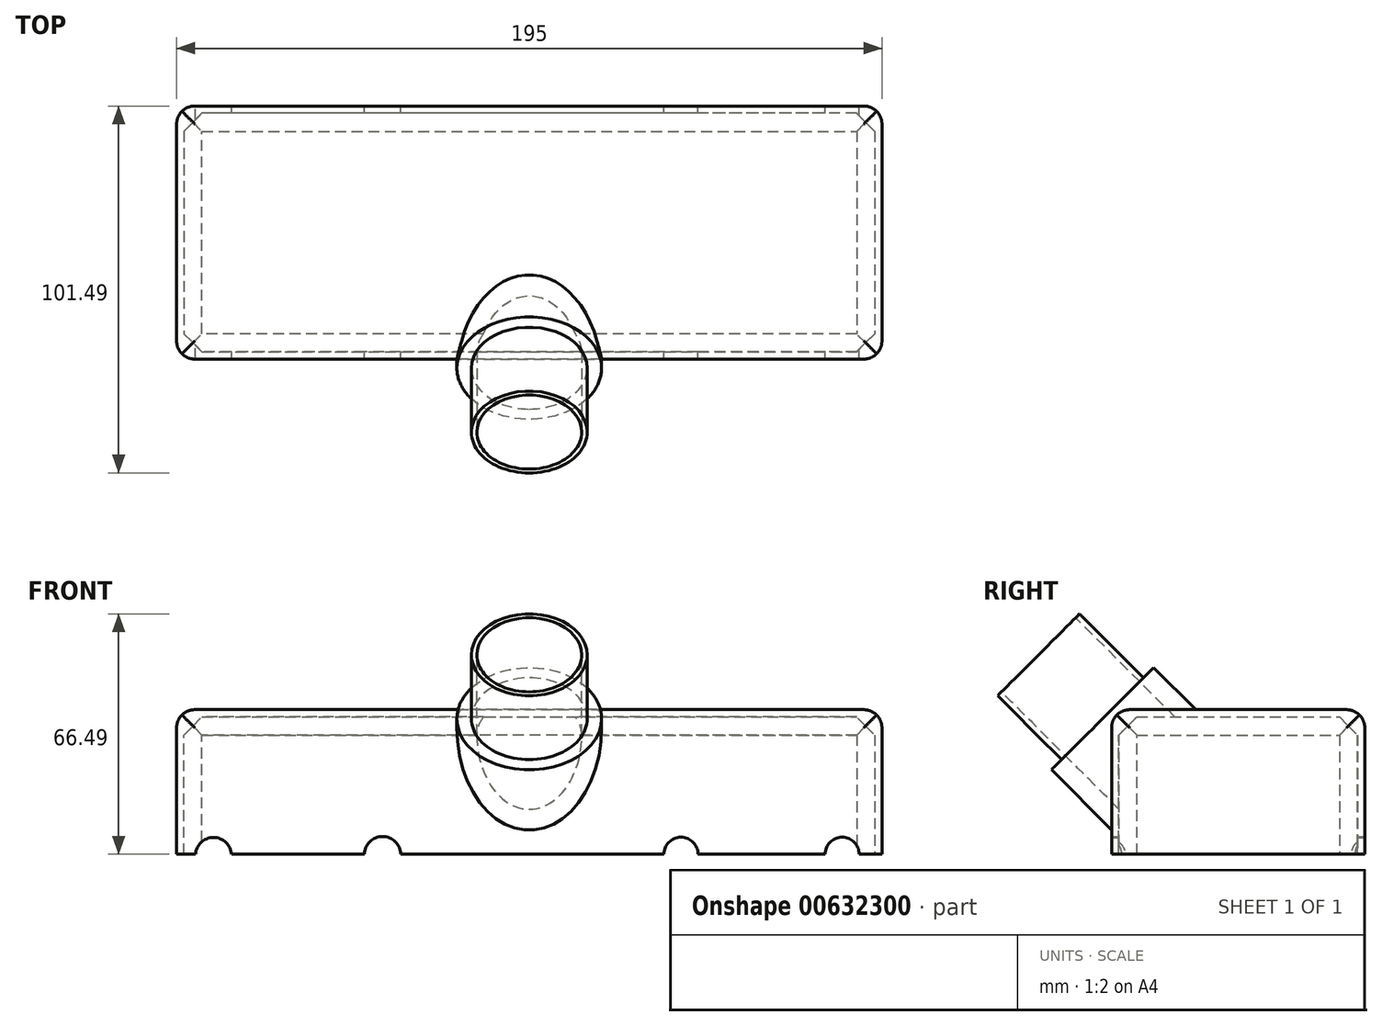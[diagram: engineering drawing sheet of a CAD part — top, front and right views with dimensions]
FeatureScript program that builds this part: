
annotation { "Feature Type Name" : "Feature", "Feature Type Description" : "" }
export const myFeature = defineFeature(function(context is Context, id is Id, definition is map)
    precondition{}
    {
        {
            var Q0;
            Q0=qCreatedBy(makeId("Top.planeOp"),FACE);
            var sketch = newSketch(context, id + "F0", { "sketchPlane" : qUnion([Q0])});
            skLineSegment(sketch, "E0.bottom", {"start": v(-97.5, -35) * mm, "end": v(97.5, -35) * mm});
            skLineSegment(sketch, "E0.top", {"start": v(-97.5, 35) * mm, "end": v(97.5, 35) * mm});
            skLineSegment(sketch, "E0.left", {"start": v(-97.5, -35) * mm, "end": v(-97.5, 35) * mm});
            skLineSegment(sketch, "E0.right", {"start": v(97.5, -35) * mm, "end": v(97.5, 35) * mm});
            skPoint(sketch, "E0.middle", {"position": v(0, 0) * mm});
            skSolve(sketch);
        }
        {
            var Q0;
            Q0=makeQuery(id+"F0.imprint","IMPRINT",FACE,{"disambiguationData":[TD([[makeQuery(id+"F0.imprint","IMPRINT",EDGE,{"derivedFrom":sQuery(id+"F0.wireOp",EDGE,"E0.bottom")}),1.0]])]});
            extrude(context, id + "F1", {"entities" : qUnion([Q0]), "depth" : 40 * mm, "offsetDistance" : 25 * mm});
        }
        {
            var Q0;
            Q0=makeQuery(id+"F1.opExtrude","CAP_EDGE",EDGE,{"disambiguationData":[OSD([sQuery(id+"F0.wireOp",EDGE,"E0.bottom")])],"isStart":false});
            cPlane(context, id + "F2", {"entities" : qUnion([Q0]), "cplaneType" : CPlaneType.LINE_ANGLE, "offset" : 25 * mm, "angle" : 45 * degree, "oppositeDirection" : true, "width" : 150 * mm, "height" : 150 * mm});
        }
        {
            var Q0;
            Q0=qCreatedBy(id+"F2.planeOp",FACE);
            var sketch = newSketch(context, id + "F3", { "sketchPlane" : qUnion([Q0])});
            skCircle(sketch, "E1", {"center": v(0, 0) * mm, "radius": 20 * mm});
            skSolve(sketch);
        }
        {
            var Q0;
            Q0=makeQuery(id+"F3.imprint","IMPRINT",FACE,{"disambiguationData":[TD([[makeQuery(id+"F3.imprint","IMPRINT",EDGE,{"derivedFrom":sQuery(id+"F3.wireOp",EDGE,"E1")}),1.0]])]});
            extrude(context, id + "F4", {"entities" : qUnion([Q0]), "operationType" : NewBodyOperationType.ADD, "depth" : 30 * mm, "offsetDistance" : 25 * mm});
        }
        {
            var Q0;
            Q0=makeQuery(id+"F4.opExtrude","CAP_FACE",FACE,{"disambiguationData":[OSD([sQuery(id+"F3.wireOp",EDGE,"E1")])],"isStart":true});
            var sketch = newSketch(context, id + "F5", { "sketchPlane" : qUnion([Q0])});
            skCircle(sketch, "E2", {"center": v(0, 0) * mm, "radius": 16 * mm});
            skSolve(sketch);
        }
        {
            var Q0;
            Q0=makeQuery(id+"F5.imprint","IMPRINT",FACE,{"disambiguationData":[TD([[makeQuery(id+"F5.imprint","IMPRINT",EDGE,{"derivedFrom":sQuery(id+"F5.wireOp",EDGE,"E2")}),1.0]])]});
            var Q1;
            Q1=makeQuery(id+"F5.imprint","IMPRINT",FACE,{"disambiguationData":[TD([[makeQuery(id+"F5.imprint","IMPRINT",EDGE,{"derivedFrom":sQuery(id+"F5.wireOp",EDGE,"E2")}),-1.0]])]});
            extrude(context, id + "F6", {"entities" : qUnion([Q0, Q1]), "operationType" : NewBodyOperationType.ADD, "depth" : 25 * mm, "offsetDistance" : 25 * mm});
        }
        {
            var Q0;
            Q0=makeQuery(id+"F6.opExtrude","CAP_FACE",FACE,{"disambiguationData":[OSD([sQuery(id+"F3.wireOp",EDGE,"E1")])],"isStart":false});
            var sketch = newSketch(context, id + "F7", { "sketchPlane" : qUnion([Q0])});
            skCircle(sketch, "E3", {"center": v(0, 0) * mm, "radius": 16 * mm});
            skSolve(sketch);
        }
        {
            var Q0;
            Q0=makeQuery(id+"F7.imprint","IMPRINT",FACE,{"disambiguationData":[TD([[makeQuery(id+"F7.imprint","IMPRINT",EDGE,{"derivedFrom":sQuery(id+"F7.wireOp",EDGE,"E3")}),-1.0]])]});
            extrude(context, id + "F8", {"entities" : qUnion([Q0]), "operationType" : NewBodyOperationType.REMOVE, "oppositeDirection" : true, "depth" : 35 * mm, "offsetDistance" : 25 * mm});
        }
        {
            var Q0;
            Q0=makeQuery(id+"F8.boolean.opBoolean","COPY",FACE,{"derivedFrom":makeQuery(id+"F8.opExtrude","CAP_FACE",FACE,{"disambiguationData":[OSD([sQuery(id+"F3.wireOp",EDGE,"E1"),sQuery(id+"F7.wireOp",EDGE,"E3")])],"isStart":false})});
            extrude(context, id + "F9", {"entities" : qUnion([Q0]), "operationType" : NewBodyOperationType.ADD, "depth" : 10 * mm, "offsetDistance" : 25 * mm});
        }
        {
            var Q0;
            Q0=makeQuery(id+"F6.opExtrude","CAP_FACE",FACE,{"disambiguationData":[OSD([sQuery(id+"F3.wireOp",EDGE,"E1")])],"isStart":false});
            var sketch = newSketch(context, id + "F10", { "sketchPlane" : qUnion([Q0])});
            skCircle(sketch, "E4", {"center": v(0, 0) * mm, "radius": 14.5 * mm});
            skSolve(sketch);
        }
        {
            var Q0;
            Q0=makeQuery(id+"F10.imprint","IMPRINT",FACE,{"disambiguationData":[TD([[makeQuery(id+"F10.imprint","IMPRINT",EDGE,{"derivedFrom":sQuery(id+"F10.wireOp",EDGE,"E4")}),1.0]])]});
            extrude(context, id + "F11", {"entities" : qUnion([Q0]), "operationType" : NewBodyOperationType.REMOVE, "endBound" : BoundingType.THROUGH_ALL, "oppositeDirection" : true, "depth" : 25 * mm, "offsetDistance" : 25 * mm});
        }
        {
            var Q0;
            Q0=makeQuery(id+"F1.opExtrude","CAP_FACE",FACE,{"disambiguationData":[OSD([sQuery(id+"F0.wireOp",EDGE,"E0.bottom"),sQuery(id+"F0.wireOp",EDGE,"E0.top"),sQuery(id+"F0.wireOp",EDGE,"E0.left"),sQuery(id+"F0.wireOp",EDGE,"E0.right")])],"isStart":true});
            var sketch = newSketch(context, id + "F12", { "sketchPlane" : qUnion([Q0])});
            skLineSegment(sketch, "E5.bottom", {"start": v(95.5, -33) * mm, "end": v(-95.5, -33) * mm});
            skLineSegment(sketch, "E5.top", {"start": v(95.5, 33) * mm, "end": v(-95.5, 33) * mm});
            skLineSegment(sketch, "E5.left", {"start": v(95.5, -33) * mm, "end": v(95.5, 33) * mm});
            skLineSegment(sketch, "E5.right", {"start": v(-95.5, -33) * mm, "end": v(-95.5, 33) * mm});
            skPoint(sketch, "E5.middle", {"position": v(0, 0) * mm});
            skSolve(sketch);
        }
        {
            var Q0;
            Q0=makeQuery(id+"F12.imprint","IMPRINT",FACE,{"disambiguationData":[TD([[makeQuery(id+"F12.imprint","IMPRINT",EDGE,{"derivedFrom":sQuery(id+"F12.wireOp",EDGE,"E5.bottom")}),-1.0]])]});
            extrude(context, id + "F13", {"entities" : qUnion([Q0]), "operationType" : NewBodyOperationType.REMOVE, "oppositeDirection" : true, "depth" : 38 * mm, "offsetDistance" : 25 * mm});
        }
        {
            var Q0;
            Q0=qCreatedBy(makeId("Top.planeOp"),FACE);
            var sketch = newSketch(context, id + "F14", { "sketchPlane" : qUnion([Q0])});
            skCircle(sketch, "E6", {"center": v(0, 0) * mm, "radius": 21.11 * mm});
            skSolve(sketch);
        }
        {
            var Q0;
            Q0 = qSketchRegion(id + "F14", true);
            extrude(context, id + "F15", {"entities" : qUnion([Q0]), "operationType" : NewBodyOperationType.REMOVE, "depth" : 38 * mm, "offsetDistance" : 25 * mm});
        }
        {
            var Q0;
            Q0=makeQuery(id+"F1.opExtrude","CAP_EDGE",EDGE,{"disambiguationData":[OSD([sQuery(id+"F0.wireOp",EDGE,"E0.top")])],"isStart":false});
            var Q1;
            Q1=makeQuery(id+"F1.opExtrude","CAP_EDGE",EDGE,{"disambiguationData":[OSD([sQuery(id+"F0.wireOp",EDGE,"E0.left")])],"isStart":false});
            var Q2;
            {var subQ1=sQuery(id+"F0.wireOp",EDGE,"E0.left");var subQ2=sQuery(id+"F0.wireOp",EDGE,"E0.bottom");Q2=makeQuery(id+"F4.boolean.opBoolean","SPLIT",EDGE,{"disambiguationData":[TD([makeQuery(id+"F1.opExtrude","SWEPT_FACE",FACE,{"disambiguationData":[OSD([subQ1])]})])],"derivedFrom":makeQuery(id+"F1.opExtrude","CAP_EDGE",EDGE,{"disambiguationData":[OSD([subQ2])],"isStart":false})});}
            var Q3;
            {var subQ1=sQuery(id+"F0.wireOp",EDGE,"E0.right");var subQ2=sQuery(id+"F0.wireOp",EDGE,"E0.bottom");Q3=makeQuery(id+"F4.boolean.opBoolean","SPLIT",EDGE,{"disambiguationData":[TD([makeQuery(id+"F1.opExtrude","SWEPT_FACE",FACE,{"disambiguationData":[OSD([subQ1])]})])],"derivedFrom":makeQuery(id+"F1.opExtrude","CAP_EDGE",EDGE,{"disambiguationData":[OSD([subQ2])],"isStart":false})});}
            var Q4;
            Q4=makeQuery(id+"F1.opExtrude","CAP_EDGE",EDGE,{"disambiguationData":[OSD([sQuery(id+"F0.wireOp",EDGE,"E0.right")])],"isStart":false});
            fillet(context, id + "F16", {"entities" : qUnion([Q0, Q1, Q2, Q3, Q4]), "radius" : 5 * mm, "tangentPropagation" : true, "allowEdgeOverflow" : false});
        }
        {
            var Q0;
            Q0=makeQuery(id+"F1.opExtrude","SWEPT_EDGE",EDGE,{"disambiguationData":[OSD([sQuery(id+"F0.wireOp",EDGE,"E0.bottom"),sQuery(id+"F0.wireOp",EDGE,"E0.right")])]});
            var Q1;
            Q1=makeQuery(id+"F1.opExtrude","SWEPT_EDGE",EDGE,{"disambiguationData":[OSD([sQuery(id+"F0.wireOp",EDGE,"E0.top"),sQuery(id+"F0.wireOp",EDGE,"E0.right")])]});
            var Q2;
            Q2=makeQuery(id+"F1.opExtrude","SWEPT_EDGE",EDGE,{"disambiguationData":[OSD([sQuery(id+"F0.wireOp",EDGE,"E0.top"),sQuery(id+"F0.wireOp",EDGE,"E0.left")])]});
            var Q3;
            Q3=makeQuery(id+"F1.opExtrude","SWEPT_EDGE",EDGE,{"disambiguationData":[OSD([sQuery(id+"F0.wireOp",EDGE,"E0.bottom"),sQuery(id+"F0.wireOp",EDGE,"E0.left")])]});
            fillet(context, id + "F17", {"entities" : qUnion([Q0, Q1, Q2, Q3]), "radius" : 5 * mm, "allowEdgeOverflow" : false});
        }
        {
            var Q0;
            {var subQ1=sQuery(id+"F12.wireOp",EDGE,"E5.right");var subQ2=sQuery(id+"F12.wireOp",EDGE,"E5.top");Q0=makeQuery(id+"F13.boolean.opBoolean","COPY",EDGE,{"disambiguationData":[TD([makeQuery(id+"F13.opExtrude","SWEPT_FACE",FACE,{"disambiguationData":[OSD([subQ1])]})])],"derivedFrom":makeQuery(id+"F13.opExtrude","CAP_EDGE",EDGE,{"disambiguationData":[OSD([subQ2])],"isStart":false})});}
            var Q1;
            Q1=makeQuery(id+"F13.boolean.opBoolean","COPY",EDGE,{"derivedFrom":makeQuery(id+"F13.opExtrude","CAP_EDGE",EDGE,{"disambiguationData":[OSD([sQuery(id+"F12.wireOp",EDGE,"E5.right")])],"isStart":false})});
            var Q2;
            Q2=makeQuery(id+"F13.boolean.opBoolean","COPY",EDGE,{"derivedFrom":makeQuery(id+"F13.opExtrude","CAP_EDGE",EDGE,{"disambiguationData":[OSD([sQuery(id+"F12.wireOp",EDGE,"E5.left")])],"isStart":false})});
            var Q3;
            {var subQ1=sQuery(id+"F12.wireOp",EDGE,"E5.left");var subQ2=sQuery(id+"F12.wireOp",EDGE,"E5.top");Q3=makeQuery(id+"F13.boolean.opBoolean","COPY",EDGE,{"disambiguationData":[TD([makeQuery(id+"F13.opExtrude","SWEPT_FACE",FACE,{"disambiguationData":[OSD([subQ1])]})])],"derivedFrom":makeQuery(id+"F13.opExtrude","CAP_EDGE",EDGE,{"disambiguationData":[OSD([subQ2])],"isStart":false})});}
            var Q4;
            Q4=makeQuery(id+"F13.boolean.opBoolean","COPY",EDGE,{"derivedFrom":makeQuery(id+"F13.opExtrude","CAP_EDGE",EDGE,{"disambiguationData":[OSD([sQuery(id+"F12.wireOp",EDGE,"E5.bottom")])],"isStart":false})});
            chamfer(context, id + "F18", {"entities" : qUnion([Q0, Q1, Q2, Q3, Q4]), "width" : 5 * mm, "tangentPropagation" : true});
        }
        {
            var Q0;
            Q0=makeQuery(id+"F13.boolean.opBoolean","COPY",EDGE,{"derivedFrom":makeQuery(id+"F13.opExtrude","SWEPT_EDGE",EDGE,{"disambiguationData":[OSD([sQuery(id+"F12.wireOp",EDGE,"E5.bottom"),sQuery(id+"F12.wireOp",EDGE,"E5.right")])]})});
            var Q1;
            Q1=makeQuery(id+"F13.boolean.opBoolean","COPY",EDGE,{"derivedFrom":makeQuery(id+"F13.opExtrude","SWEPT_EDGE",EDGE,{"disambiguationData":[OSD([sQuery(id+"F12.wireOp",EDGE,"E5.bottom"),sQuery(id+"F12.wireOp",EDGE,"E5.left")])]})});
            var Q2;
            Q2=makeQuery(id+"F13.boolean.opBoolean","COPY",EDGE,{"derivedFrom":makeQuery(id+"F13.opExtrude","SWEPT_EDGE",EDGE,{"disambiguationData":[OSD([sQuery(id+"F12.wireOp",EDGE,"E5.top"),sQuery(id+"F12.wireOp",EDGE,"E5.right")])]})});
            var Q3;
            Q3=makeQuery(id+"F13.boolean.opBoolean","COPY",EDGE,{"derivedFrom":makeQuery(id+"F13.opExtrude","SWEPT_EDGE",EDGE,{"disambiguationData":[OSD([sQuery(id+"F12.wireOp",EDGE,"E5.top"),sQuery(id+"F12.wireOp",EDGE,"E5.left")])]})});
            chamfer(context, id + "F19", {"entities" : qUnion([Q0, Q1, Q2, Q3]), "width" : 5 * mm, "tangentPropagation" : true});
        }
        {
            var Q0;
            Q0=makeQuery(id+"F1.opExtrude","SWEPT_FACE",FACE,{"disambiguationData":[OSD([sQuery(id+"F0.wireOp",EDGE,"E0.top")])]});
            var sketch = newSketch(context, id + "F20", { "sketchPlane" : qUnion([Q0])});
            skCircle(sketch, "E7", {"center": v(-86.5, 0) * mm, "radius": 4.72 * mm});
            skCircle(sketch, "E8", {"center": v(-75.5, 0) * mm, "radius": 4.78 * mm});
            skCircle(sketch, "E9", {"center": v(-63.68, 0) * mm, "radius": 4.72 * mm});
            skCircle(sketch, "E10", {"center": v(-52.95, 0) * mm, "radius": 5 * mm});
            skCircle(sketch, "E11", {"center": v(52.66, -0.33) * mm, "radius": 4.72 * mm});
            skCircle(sketch, "E12", {"center": v(64.21, -0.33) * mm, "radius": 4.78 * mm});
            skCircle(sketch, "E13", {"center": v(75.76, -0.33) * mm, "radius": 4.72 * mm});
            skCircle(sketch, "E14", {"center": v(87.31, -0.33) * mm, "radius": 5 * mm});
            skCircle(sketch, "E15", {"center": v(5.91, -0.06) * mm, "radius": 4.72 * mm});
            skCircle(sketch, "E16", {"center": v(17.46, -0.06) * mm, "radius": 4.78 * mm});
            skCircle(sketch, "E17", {"center": v(29.01, -0.06) * mm, "radius": 4.72 * mm});
            skCircle(sketch, "E18", {"center": v(40.56, -0.06) * mm, "radius": 5 * mm});
            skCircle(sketch, "E19", {"center": v(-41.94, 0) * mm, "radius": 4.72 * mm});
            skCircle(sketch, "E20", {"center": v(-30.67, 0) * mm, "radius": 4.78 * mm});
            skCircle(sketch, "E21", {"center": v(-19.94, 0) * mm, "radius": 4.72 * mm});
            skCircle(sketch, "E22", {"center": v(-8.1, 0) * mm, "radius": 5 * mm});
            skSolve(sketch);
        }
        {
            var Q0;
            {var subQ0=sQuery(id+"F20.wireOp",EDGE,"E7");var subQ1=makeQuery(id+"F1.opExtrude","CAP_EDGE",EDGE,{"disambiguationData":[OSD([sQuery(id+"F0.wireOp",EDGE,"E0.top")])],"isStart":true});var subQ2=makeQuery(id+"F20.imprint","INTERSECT",VERTEX,{"disambiguationData":[OD(0.0)],"derivedFrom":[subQ1,subQ0]});Q0=makeQuery(id+"F20.imprint","IMPRINT",FACE,{"disambiguationData":[TD([[makeQuery(id+"F20.imprint","IMPRINT",EDGE,{"disambiguationData":[TD([[subQ2,1.0]])],"derivedFrom":subQ0}),1.0]])]});}
            var Q1;
            {var subQ0=sQuery(id+"F20.wireOp",EDGE,"E14");var subQ1=makeQuery(id+"F1.opExtrude","CAP_EDGE",EDGE,{"disambiguationData":[OSD([sQuery(id+"F0.wireOp",EDGE,"E0.top")])],"isStart":true});var subQ2=makeQuery(id+"F20.imprint","INTERSECT",VERTEX,{"disambiguationData":[OD(0.0)],"derivedFrom":[subQ1,subQ0]});Q1=makeQuery(id+"F20.imprint","IMPRINT",FACE,{"disambiguationData":[TD([[makeQuery(id+"F20.imprint","IMPRINT",EDGE,{"disambiguationData":[TD([[subQ2,-1.0]])],"derivedFrom":subQ0}),1.0]])]});}
            var Q2;
            {var subQ0=sQuery(id+"F20.wireOp",EDGE,"E19");var subQ1=makeQuery(id+"F1.opExtrude","CAP_EDGE",EDGE,{"disambiguationData":[OSD([sQuery(id+"F0.wireOp",EDGE,"E0.top")])],"isStart":true});var subQ2=makeQuery(id+"F20.imprint","INTERSECT",VERTEX,{"disambiguationData":[OD(0.0)],"derivedFrom":[subQ1,subQ0]});Q2=makeQuery(id+"F20.imprint","IMPRINT",FACE,{"disambiguationData":[TD([[makeQuery(id+"F20.imprint","IMPRINT",EDGE,{"disambiguationData":[TD([[subQ2,1.0]])],"derivedFrom":subQ0}),1.0]])]});}
            var Q3;
            {var subQ0=sQuery(id+"F20.wireOp",EDGE,"E18");var subQ1=makeQuery(id+"F1.opExtrude","CAP_EDGE",EDGE,{"disambiguationData":[OSD([sQuery(id+"F0.wireOp",EDGE,"E0.top")])],"isStart":true});var subQ2=makeQuery(id+"F20.imprint","INTERSECT",VERTEX,{"disambiguationData":[OD(0.0)],"derivedFrom":[subQ1,subQ0]});Q3=makeQuery(id+"F20.imprint","IMPRINT",FACE,{"disambiguationData":[TD([[makeQuery(id+"F20.imprint","IMPRINT",EDGE,{"disambiguationData":[TD([[subQ2,-1.0]])],"derivedFrom":subQ0}),1.0]])]});}
            extrude(context, id + "F21", {"entities" : qUnion([Q0, Q1, Q2, Q3]), "operationType" : NewBodyOperationType.REMOVE, "endBound" : BoundingType.THROUGH_ALL, "oppositeDirection" : true, "depth" : 25 * mm, "offsetDistance" : 25 * mm});
        }
    });
